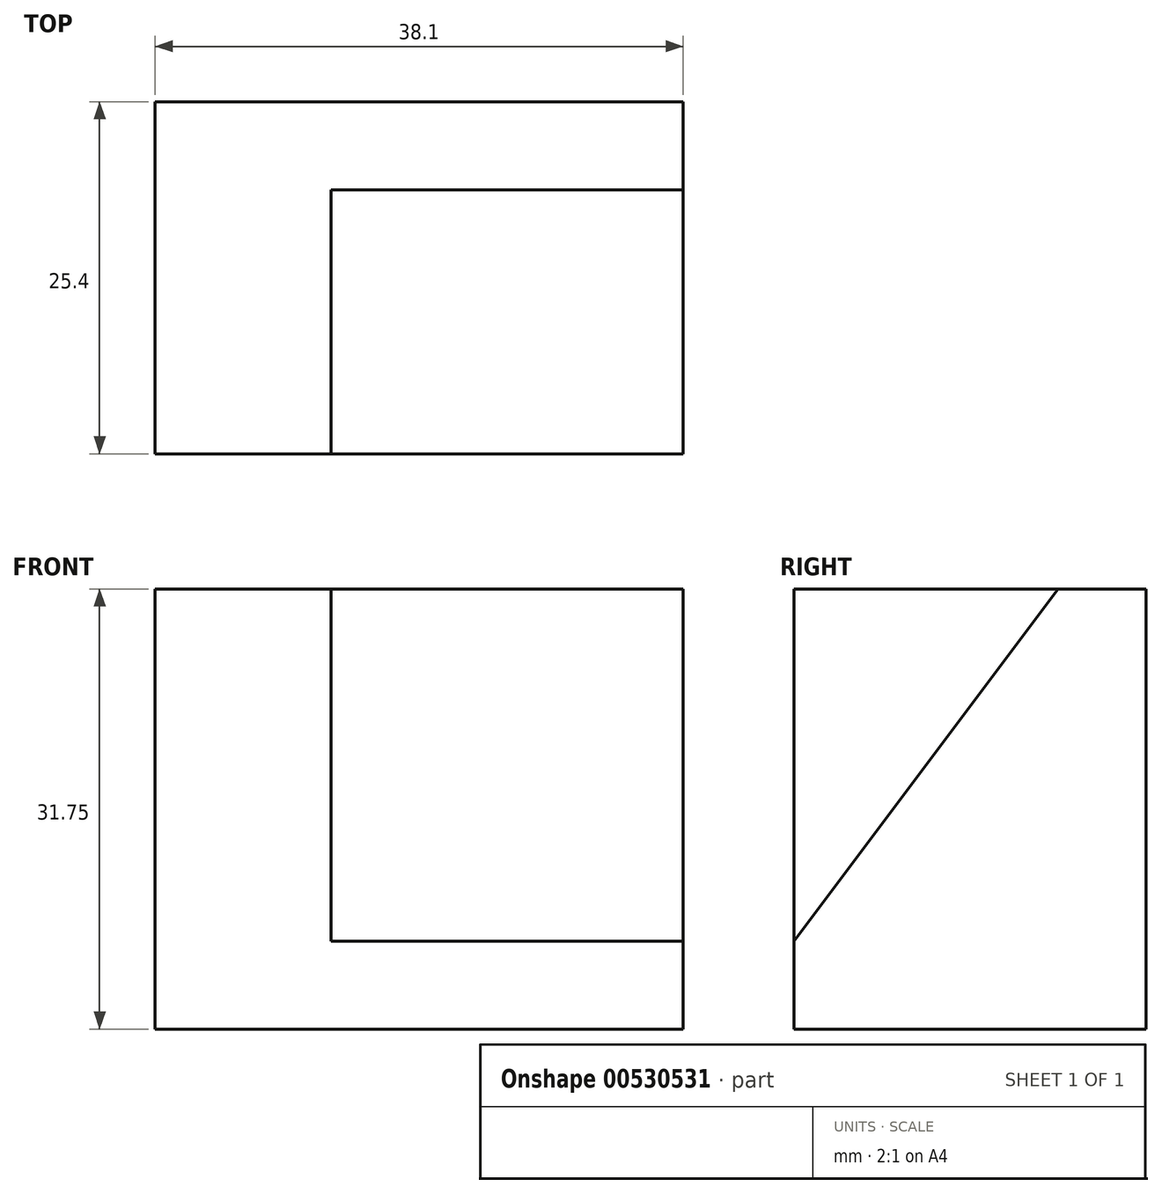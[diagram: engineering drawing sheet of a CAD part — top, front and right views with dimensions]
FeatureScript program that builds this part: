
annotation { "Feature Type Name" : "Feature", "Feature Type Description" : "" }
export const myFeature = defineFeature(function(context is Context, id is Id, definition is map)
    precondition{}
    {
        {
            var Q0;
            Q0=qCreatedBy(makeId("Front.planeOp"),FACE);
            var sketch = newSketch(context, id + "F0", { "sketchPlane" : qUnion([Q0])});
            skLineSegment(sketch, "E0", {"start": v(-64.17, 0) * mm, "end": v(-64.17, 31.75) * mm});
            skLineSegment(sketch, "E1", {"start": v(-64.17, 31.75) * mm, "end": v(-26.07, 31.75) * mm});
            skLineSegment(sketch, "E2", {"start": v(-26.07, 31.75) * mm, "end": v(-26.07, 0) * mm});
            skLineSegment(sketch, "E3", {"start": v(-26.07, 0) * mm, "end": v(-64.17, 0) * mm});
            skSolve(sketch);
        }
        {
            var Q0;
            Q0=makeQuery(id+"F0.imprint","IMPRINT",FACE,{"disambiguationData":[TD([[makeQuery(id+"F0.imprint","IMPRINT",EDGE,{"derivedFrom":sQuery(id+"F0.wireOp",EDGE,"E0")}),-1.0]])]});
            extrude(context, id + "F1", {"entities" : qUnion([Q0]), "depth" : 25.4 * mm, "offsetDistance" : 25.4 * mm});
        }
        {
            var Q0;
            Q0=makeQuery(id+"F1.opExtrude","SWEPT_FACE",FACE,{"disambiguationData":[OSD([sQuery(id+"F0.wireOp",EDGE,"E2")])]});
            var sketch = newSketch(context, id + "F2", { "sketchPlane" : qUnion([Q0])});
            skLineSegment(sketch, "E4", {"start": v(-6.35, 31.75) * mm, "end": v(-25.4, 6.35) * mm});
            skSolve(sketch);
        }
        {
            var Q0;
            Q0 = qSketchRegion(id + "F2", true);
            var Q1;
            {var subQ0=sQuery(id+"F2.wireOp",EDGE,"E4");Q1=makeQuery(id+"F2.imprint","IMPRINT",FACE,{"disambiguationData":[TD([[makeQuery(id+"F2.imprint","IMPRINT",EDGE,{"derivedFrom":subQ0}),-1.0]])]});}
            extrude(context, id + "F3", {"entities" : qUnion([Q0, Q1]), "operationType" : NewBodyOperationType.REMOVE, "oppositeDirection" : true, "depth" : 25.4 * mm, "offsetDistance" : 25.4 * mm});
        }
    });
